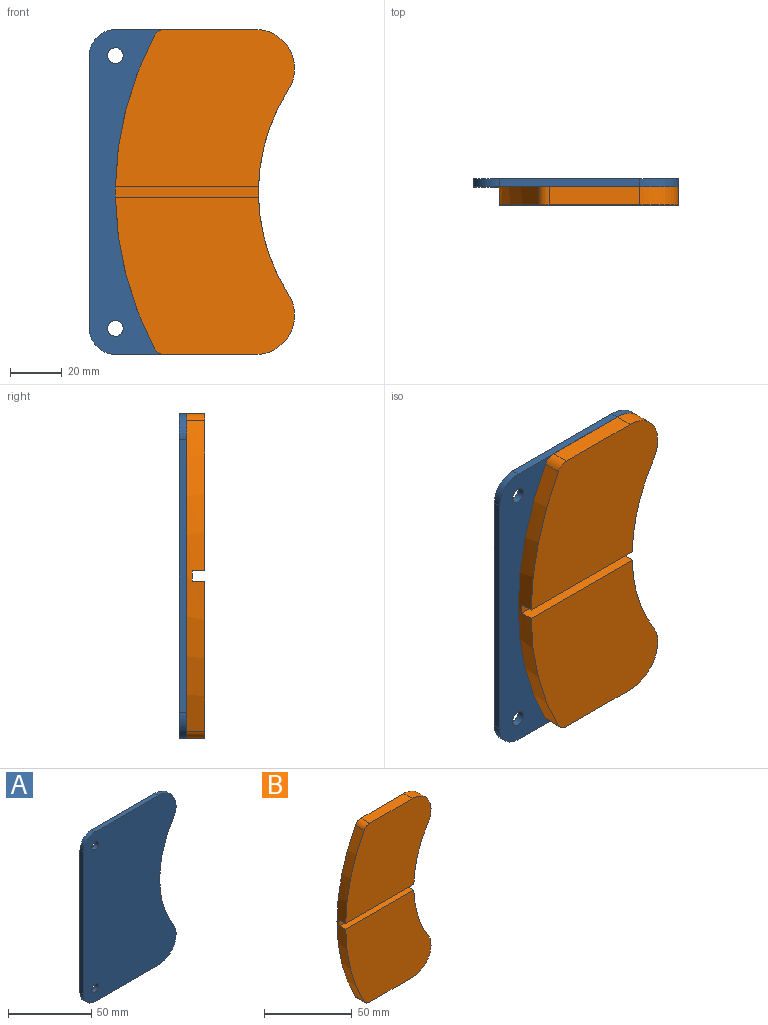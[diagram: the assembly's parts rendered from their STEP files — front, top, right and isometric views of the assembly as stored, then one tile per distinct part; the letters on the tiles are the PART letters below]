
ASSEMBLY  parts=2 mates=1
PART A: 12 faces, bbox 78.9x3x125 mm
  f0: plane 53.92x3mm, normal (0,0,1), area 161.8mm2, adj f1,f8,f10,f11
  f1: cylinder r=10mm len=10mm, axis (0,-1,0), area 47.1mm2, adj f0,f2,f10,f11
  f2: plane 105x3mm, normal (-1,0,0), area 315mm2, adj f1,f3,f10,f11
  f3: cylinder r=10mm len=10mm, axis (0,-1,0), area 47.1mm2, adj f2,f4,f10,f11
  f4: plane 53.92x3mm, normal (0,0,-1), area 161.8mm2, adj f3,f5,f10,f11
  f5: cylinder r=15mm len=23.1mm, axis (0,-1,0), area 96.3mm2, adj f4,f6,f10,f11
  f6: cylinder r=73mm len=78.81mm, axis (0,-1,0), area 249.7mm2, adj f5,f8,f10,f11
  f7: cylinder r=3mm len=6mm, axis (0,-1,0), area 56.5mm2, adj f10,f11
  f8: cylinder r=15mm len=23.1mm, axis (0,-1,0), area 96.3mm2, adj f0,f6,f10,f11
  f9: cylinder r=3mm len=6mm, axis (0,-1,0), area 56.5mm2, adj f10,f11
  f10: plane 125x78.92mm, normal (0,1,0), area 8852.7mm2, adj f0,f1,f2,f3,f4,f5,f6,f7
  f11: plane 125x78.92mm, normal (0,-1,0), area 8852.7mm2, adj f0,f1,f2,f3,f4,f5,f6,f7
PART B: 14 faces, bbox 68.9x7x125 mm
  f0: plane 68.91x60.5mm, normal (0,-1,0), area 3409.2mm2, adj f1,f2,f3,f4,f8,f11
  f1: cylinder r=73mm len=78.81mm, axis (0,-1,0), area 562.7mm2, adj f0,f7,f8,f9,f10,f11,f12,f13
  f2: plane 34.65x7mm, normal (0,0,1), area 242.6mm2, adj f0,f3,f8,f9
  f3: cylinder r=5mm len=7mm, axis (0,-1,0), area 38mm2, adj f0,f2,f4,f9
  f4: cylinder r=128mm len=119.67mm, axis (0,-1,0), area 851.7mm2, adj f0,f3,f5,f9,f10,f11,f12,f13
  f5: cylinder r=5mm len=7mm, axis (0,-1,0), area 38mm2, adj f4,f6,f9,f10
  f6: plane 34.65x7mm, normal (0,0,-1), area 242.6mm2, adj f5,f7,f9,f10
  f7: cylinder r=15mm len=23.1mm, axis (0,-1,0), area 224.8mm2, adj f1,f6,f9,f10
  f8: cylinder r=15mm len=23.1mm, axis (0,-1,0), area 224.8mm2, adj f0,f1,f2,f9
  f9: plane 125x68.92mm, normal (0,1,0), area 7038.5mm2, adj f1,f2,f3,f4,f5,f6,f7,f8
  f10: plane 68.91x60.5mm, normal (0,-1,0), area 3409.2mm2, adj f1,f4,f5,f6,f7,f12
  f11: plane 55.01x5mm, normal (0,0,-1), area 275.1mm2, adj f0,f1,f4,f13
  f12: plane 55.01x5mm, normal (0,0,1), area 275.1mm2, adj f1,f4,f10,f13
  f13: plane 55.03x4mm, normal (0,-1,0), area 220mm2, adj f1,f4,f11,f12
PLACE A t=(68.82,0,0)mm
PLACE B t=(68.82,0,0)mm
MATE fastened A.f8 <-> B.f8  axis (0,-1,0) through (-5.26,8,47.5)mm
